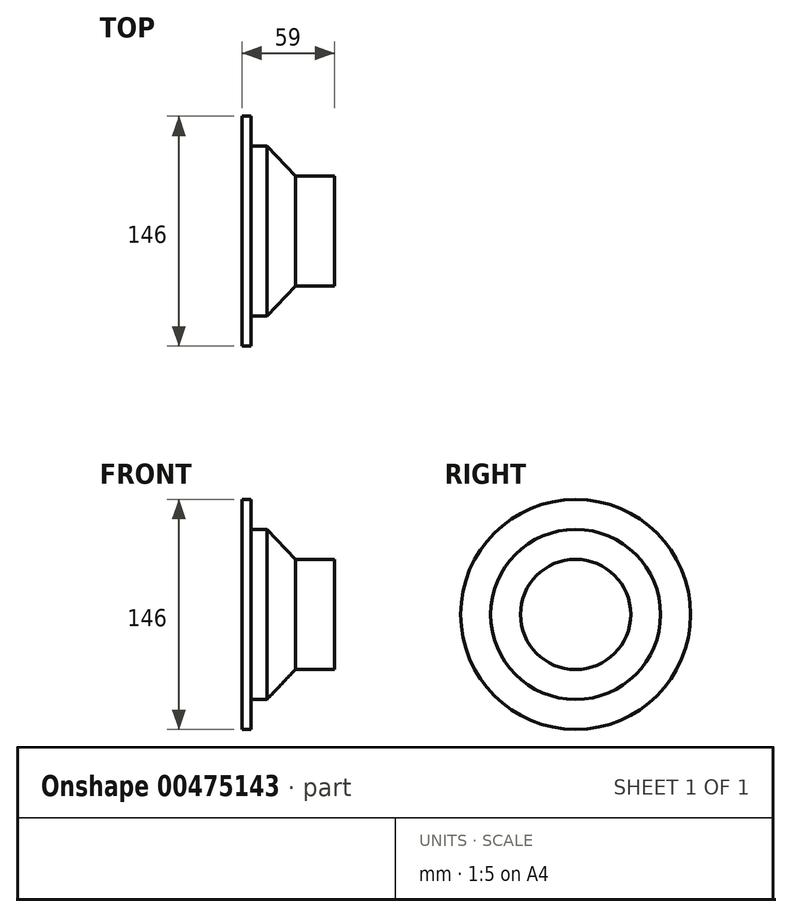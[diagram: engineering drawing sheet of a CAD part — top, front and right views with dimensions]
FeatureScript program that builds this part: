
annotation { "Feature Type Name" : "Feature", "Feature Type Description" : "" }
export const myFeature = defineFeature(function(context is Context, id is Id, definition is map)
    precondition{}
    {
        {
            var Q0;
            Q0=qCreatedBy(makeId("Front.planeOp"),FACE);
            var sketch = newSketch(context, id + "F0", { "sketchPlane" : qUnion([Q0])});
            skLineSegment(sketch, "E0", {"start": v(0, 0) * mm, "end": v(0, 73) * mm});
            skLineSegment(sketch, "E1", {"start": v(0, 73) * mm, "end": v(6, 73) * mm});
            skLineSegment(sketch, "E2", {"start": v(6, 73) * mm, "end": v(6, 54) * mm});
            skLineSegment(sketch, "E3", {"start": v(6, 54) * mm, "end": v(16, 54) * mm});
            skLineSegment(sketch, "E4", {"start": v(16, 54) * mm, "end": v(34, 35) * mm});
            skLineSegment(sketch, "E5", {"start": v(34, 35) * mm, "end": v(59, 35) * mm});
            skLineSegment(sketch, "E6", {"start": v(59, 35) * mm, "end": v(59, 0) * mm});
            skLineSegment(sketch, "E7", {"start": v(59, 0) * mm, "end": v(0, 0) * mm});
            skSolve(sketch);
        }
        {
            var Q0;
            Q0=qSketchRegion(id+"F0",true);
            var Q1;
            Q1=sQuery(id+"F0.wireOp",EDGE,"E7");
            revolve(context, id + "F1", {"entities" : qUnion([Q0]), "axis" : qUnion([Q1]), "revolveType" : RevolveType.FULL});
        }
    });
